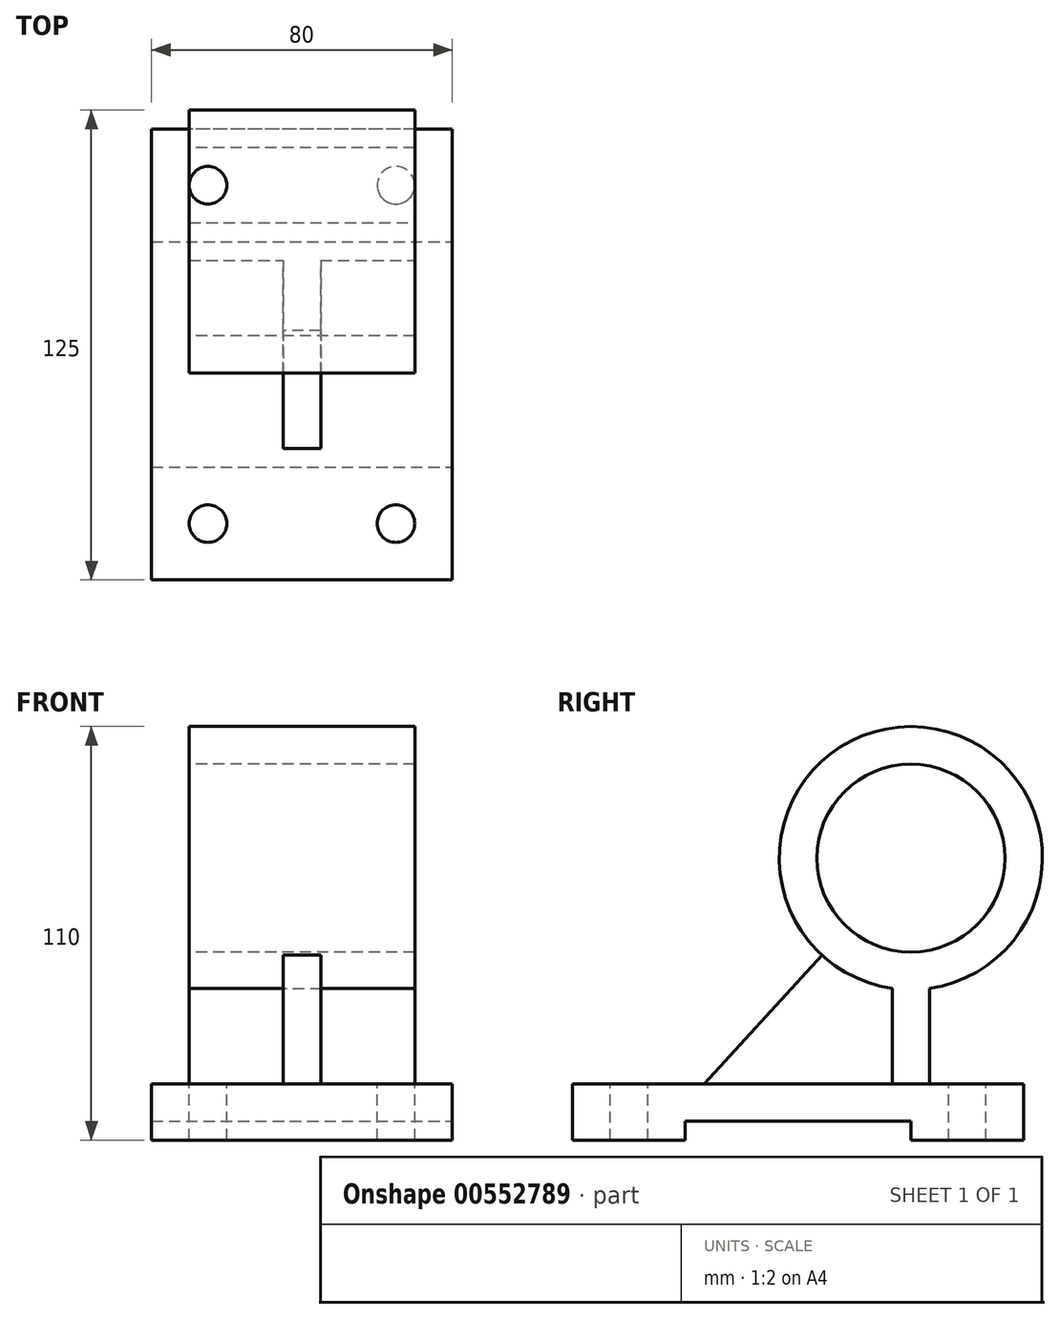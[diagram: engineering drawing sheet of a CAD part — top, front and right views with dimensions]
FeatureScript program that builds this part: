
annotation { "Feature Type Name" : "Feature", "Feature Type Description" : "" }
export const myFeature = defineFeature(function(context is Context, id is Id, definition is map)
    precondition{}
    {
        {
            var Q0;
            Q0=qCreatedBy(makeId("Right.planeOp"),FACE);
            var sketch = newSketch(context, id + "F0", { "sketchPlane" : qUnion([Q0])});
            skLineSegment(sketch, "E0", {"start": v(0, 60) * mm, "end": v(0, 0) * mm});
            skLineSegment(sketch, "E1", {"start": v(0, 0) * mm, "end": v(-55, 0) * mm});
            skLineSegment(sketch, "E2", {"start": v(-55, 0) * mm, "end": v(0, 60) * mm});
            skSolve(sketch);
        }
        {
            var Q0;
            Q0=makeQuery(id+"F0.imprint","IMPRINT",FACE,{"disambiguationData":[TD([[makeQuery(id+"F0.imprint","IMPRINT",EDGE,{"derivedFrom":sQuery(id+"F0.wireOp",EDGE,"E0")}),-1.0]])]});
            extrude(context, id + "F1", {"entities" : qUnion([Q0]), "depth" : 10 * mm, "offsetDistance" : 25 * mm});
        }
        {
            var Q0;
            Q0=makeQuery(id+"F1.opExtrude","CAP_FACE",FACE,{"disambiguationData":[OSD([sQuery(id+"F0.wireOp",EDGE,"E0"),sQuery(id+"F0.wireOp",EDGE,"E1"),sQuery(id+"F0.wireOp",EDGE,"E2")])],"isStart":false});
            var sketch = newSketch(context, id + "F2", { "sketchPlane" : qUnion([Q0])});
            skCircle(sketch, "E3", {"center": v(0, 60) * mm, "radius": 35 * mm});
            skCircle(sketch, "E4", {"center": v(0, 60) * mm, "radius": 25 * mm});
            skSolve(sketch);
        }
        {
            var Q0;
            {var subQ0=sQuery(id+"F2.wireOp",EDGE,"E3");var subQ1=makeQuery(id+"F1.opExtrude","CAP_EDGE",EDGE,{"disambiguationData":[OSD([sQuery(id+"F0.wireOp",EDGE,"E0")])],"isStart":false});var subQ2=makeQuery(id+"F2.imprint","INTERSECT",VERTEX,{"derivedFrom":[subQ1,subQ0]});Q0=makeQuery(id+"F2.imprint","IMPRINT",FACE,{"disambiguationData":[TD([[makeQuery(id+"F2.imprint","IMPRINT",EDGE,{"disambiguationData":[TD([[subQ2,-1.0]])],"derivedFrom":subQ0}),1.0]])]});}
            var Q1;
            {var subQ0=sQuery(id+"F2.wireOp",EDGE,"E3");var subQ1=makeQuery(id+"F1.opExtrude","CAP_EDGE",EDGE,{"disambiguationData":[OSD([sQuery(id+"F0.wireOp",EDGE,"E0")])],"isStart":false});var subQ2=makeQuery(id+"F2.imprint","INTERSECT",VERTEX,{"derivedFrom":[subQ1,subQ0]});Q1=makeQuery(id+"F2.imprint","IMPRINT",FACE,{"disambiguationData":[TD([[makeQuery(id+"F2.imprint","IMPRINT",EDGE,{"disambiguationData":[TD([[subQ2,1.0]])],"derivedFrom":subQ0}),1.0]])]});}
            extrude(context, id + "F3", {"entities" : qUnion([Q0, Q1]), "operationType" : NewBodyOperationType.ADD, "depth" : 25 * mm, "offsetDistance" : 25 * mm, "hasSecondDirection" : true, "secondDirectionOppositeDirection" : true, "secondDirectionDepth" : 35 * mm});
        }
        {
            var Q0;
            {var subQ0=sQuery(id+"F0.wireOp",EDGE,"E0");var subQ1=sQuery(id+"F0.wireOp",EDGE,"E2");Q0=makeQuery(id+"F3.boolean.opBoolean","SPLIT",FACE,{"disambiguationData":[TD([makeQuery(id+"F3.opExtrude","SWEPT_FACE",FACE,{"disambiguationData":[OSD([sQuery(id+"F2.wireOp",EDGE,"E4")])]})])],"derivedFrom":makeQuery(id+"F1.opExtrude","CAP_FACE",FACE,{"disambiguationData":[OSD([subQ0,sQuery(id+"F0.wireOp",EDGE,"E1"),subQ1])],"isStart":false})});}
            extrude(context, id + "F4", {"entities" : qUnion([Q0]), "operationType" : NewBodyOperationType.REMOVE, "oppositeDirection" : true, "depth" : 25 * mm, "offsetDistance" : 25 * mm});
        }
        {
            var Q0;
            Q0=makeQuery(id+"F1.opExtrude","SWEPT_FACE",FACE,{"disambiguationData":[OSD([sQuery(id+"F0.wireOp",EDGE,"E1")])]});
            var sketch = newSketch(context, id + "F5", { "sketchPlane" : qUnion([Q0])});
            skLineSegment(sketch, "E5.bottom", {"start": v(45, 90) * mm, "end": v(-35, 90) * mm});
            skLineSegment(sketch, "E5.top", {"start": v(45, -30) * mm, "end": v(-35, -30) * mm});
            skLineSegment(sketch, "E5.left", {"start": v(45, 90) * mm, "end": v(45, -30) * mm});
            skLineSegment(sketch, "E5.right", {"start": v(-35, 90) * mm, "end": v(-35, -30) * mm});
            skSolve(sketch);
        }
        {
            var Q0;
            Q0=makeQuery(id+"F5.imprint","IMPRINT",FACE,{"disambiguationData":[TD([[makeQuery(id+"F5.imprint","IMPRINT",EDGE,{"derivedFrom":sQuery(id+"F5.wireOp",EDGE,"E5.bottom")}),1.0]])]});
            var Q1;
            {var subQ0=sQuery(id+"F0.wireOp",EDGE,"E1");Q1=makeQuery(id+"F5.imprint","IMPRINT",FACE,{"disambiguationData":[TD([[makeQuery(id+"F5.imprint","IMPRINT",EDGE,{"derivedFrom":makeQuery(id+"F1.opExtrude","CAP_EDGE",EDGE,{"disambiguationData":[OSD([subQ0])],"isStart":true})}),-1.0]])]});}
            extrude(context, id + "F6", {"entities" : qUnion([Q0, Q1]), "operationType" : NewBodyOperationType.ADD, "depth" : 15 * mm, "offsetDistance" : 25 * mm});
        }
        {
            var Q0;
            Q0=makeQuery(id+"F3.opExtrude","CAP_FACE",FACE,{"disambiguationData":[OSD([sQuery(id+"F2.wireOp",EDGE,"E3"),sQuery(id+"F2.wireOp",EDGE,"E4")])],"isStart":false});
            var sketch = newSketch(context, id + "F7", { "sketchPlane" : qUnion([Q0])});
            skLineSegment(sketch, "E6", {"start": v(0, 95) * mm, "end": v(0, 25) * mm, "construction": true});
            skLineSegment(sketch, "E7", {"start": v(-5, 25.36) * mm, "end": v(-5, -0.83) * mm});
            skLineSegment(sketch, "E8", {"start": v(5, 25.36) * mm, "end": v(5, -1.02) * mm});
            skLineSegment(sketch, "E9.bottom", {"start": v(-5, 25.36) * mm, "end": v(5, 25.36) * mm});
            skLineSegment(sketch, "E9.top", {"start": v(-5, -1.02) * mm, "end": v(5, -1.02) * mm});
            skLineSegment(sketch, "E9.left", {"start": v(-5, 25.36) * mm, "end": v(-5, -1.02) * mm});
            skSolve(sketch);
        }
        {
            var Q0;
            {var subQ0=sQuery(id+"F7.wireOp",EDGE,"E9.top");Q0=makeQuery(id+"F7.imprint","IMPRINT",FACE,{"disambiguationData":[TD([[makeQuery(id+"F7.imprint","IMPRINT",EDGE,{"derivedFrom":subQ0}),1.0]])]});}
            var Q1;
            Q1=makeQuery(id+"F3.opExtrude","CAP_FACE",FACE,{"disambiguationData":[OSD([sQuery(id+"F2.wireOp",EDGE,"E3"),sQuery(id+"F2.wireOp",EDGE,"E4")])],"isStart":true});
            extrude(context, id + "F8", {"entities" : qUnion([Q0]), "operationType" : NewBodyOperationType.ADD, "endBound" : BoundingType.UP_TO_SURFACE, "oppositeDirection" : true, "depth" : 25 * mm, "endBoundEntityFace" : qUnion([Q1]), "offsetDistance" : 25 * mm});
        }
        {
            var Q0;
            Q0=makeQuery(id+"F6.opExtrude","SWEPT_FACE",FACE,{"disambiguationData":[OSD([sQuery(id+"F5.wireOp",EDGE,"E5.left")])]});
            var sketch = newSketch(context, id + "F9", { "sketchPlane" : qUnion([Q0])});
            skLineSegment(sketch, "E10.bottom", {"start": v(-60, -15) * mm, "end": v(0, -15) * mm});
            skLineSegment(sketch, "E10.top", {"start": v(-60, -10) * mm, "end": v(0, -10) * mm});
            skLineSegment(sketch, "E10.left", {"start": v(-60, -15) * mm, "end": v(-60, -10) * mm});
            skLineSegment(sketch, "E10.right", {"start": v(0, -15) * mm, "end": v(0, -10) * mm});
            skSolve(sketch);
        }
        {
            var Q0;
            Q0=makeQuery(id+"F9.imprint","IMPRINT",FACE,{"disambiguationData":[TD([[makeQuery(id+"F9.imprint","IMPRINT",EDGE,{"derivedFrom":sQuery(id+"F9.wireOp",EDGE,"E10.bottom")}),1.0]])]});
            extrude(context, id + "F10", {"entities" : qUnion([Q0]), "operationType" : NewBodyOperationType.REMOVE, "oppositeDirection" : true, "depth" : 80 * mm, "offsetDistance" : 25 * mm});
        }
        {
            var Q0;
            Q0=makeQuery(id+"F6.opExtrude","CAP_FACE",FACE,{"disambiguationData":[OSD([sQuery(id+"F5.wireOp",EDGE,"E5.bottom"),sQuery(id+"F5.wireOp",EDGE,"E5.top"),sQuery(id+"F5.wireOp",EDGE,"E5.left"),sQuery(id+"F5.wireOp",EDGE,"E5.right")])],"isStart":true});
            var sketch = newSketch(context, id + "F11", { "sketchPlane" : qUnion([Q0])});
            skCircle(sketch, "E11", {"center": v(30, -75) * mm, "radius": 5 * mm});
            skCircle(sketch, "E12.0.1.0", {"center": v(30, 15) * mm, "radius": 5 * mm});
            skCircle(sketch, "E12.1.0.0", {"center": v(-20, -75) * mm, "radius": 5 * mm});
            skCircle(sketch, "E12.1.1.0", {"center": v(-20, 15) * mm, "radius": 5 * mm});
            skLineSegment(sketch, "E12.direction1", {"start": v(30, -75) * mm, "end": v(-20, -75) * mm, "construction": true});
            skLineSegment(sketch, "E12.direction2", {"start": v(30, -75) * mm, "end": v(30, 15) * mm, "construction": true});
            skSolve(sketch);
        }
        {
            var Q0;
            Q0=makeQuery(id+"F11.imprint","IMPRINT",FACE,{"disambiguationData":[TD([[makeQuery(id+"F11.imprint","IMPRINT",EDGE,{"derivedFrom":sQuery(id+"F11.wireOp",EDGE,"E12.1.0.0")}),1.0]])]});
            var Q1;
            Q1=makeQuery(id+"F11.imprint","IMPRINT",FACE,{"disambiguationData":[TD([[makeQuery(id+"F11.imprint","IMPRINT",EDGE,{"derivedFrom":sQuery(id+"F11.wireOp",EDGE,"E11")}),1.0]])]});
            var Q2;
            Q2=makeQuery(id+"F11.imprint","IMPRINT",FACE,{"disambiguationData":[TD([[makeQuery(id+"F11.imprint","IMPRINT",EDGE,{"derivedFrom":sQuery(id+"F11.wireOp",EDGE,"E12.0.1.0")}),1.0]])]});
            var Q3;
            Q3=makeQuery(id+"F11.imprint","IMPRINT",FACE,{"disambiguationData":[TD([[makeQuery(id+"F11.imprint","IMPRINT",EDGE,{"derivedFrom":sQuery(id+"F11.wireOp",EDGE,"E12.1.1.0")}),1.0]])]});
            extrude(context, id + "F12", {"entities" : qUnion([Q0, Q1, Q2, Q3]), "operationType" : NewBodyOperationType.REMOVE, "oppositeDirection" : true, "depth" : 51.9 * mm, "offsetDistance" : 25 * mm});
        }
    });
